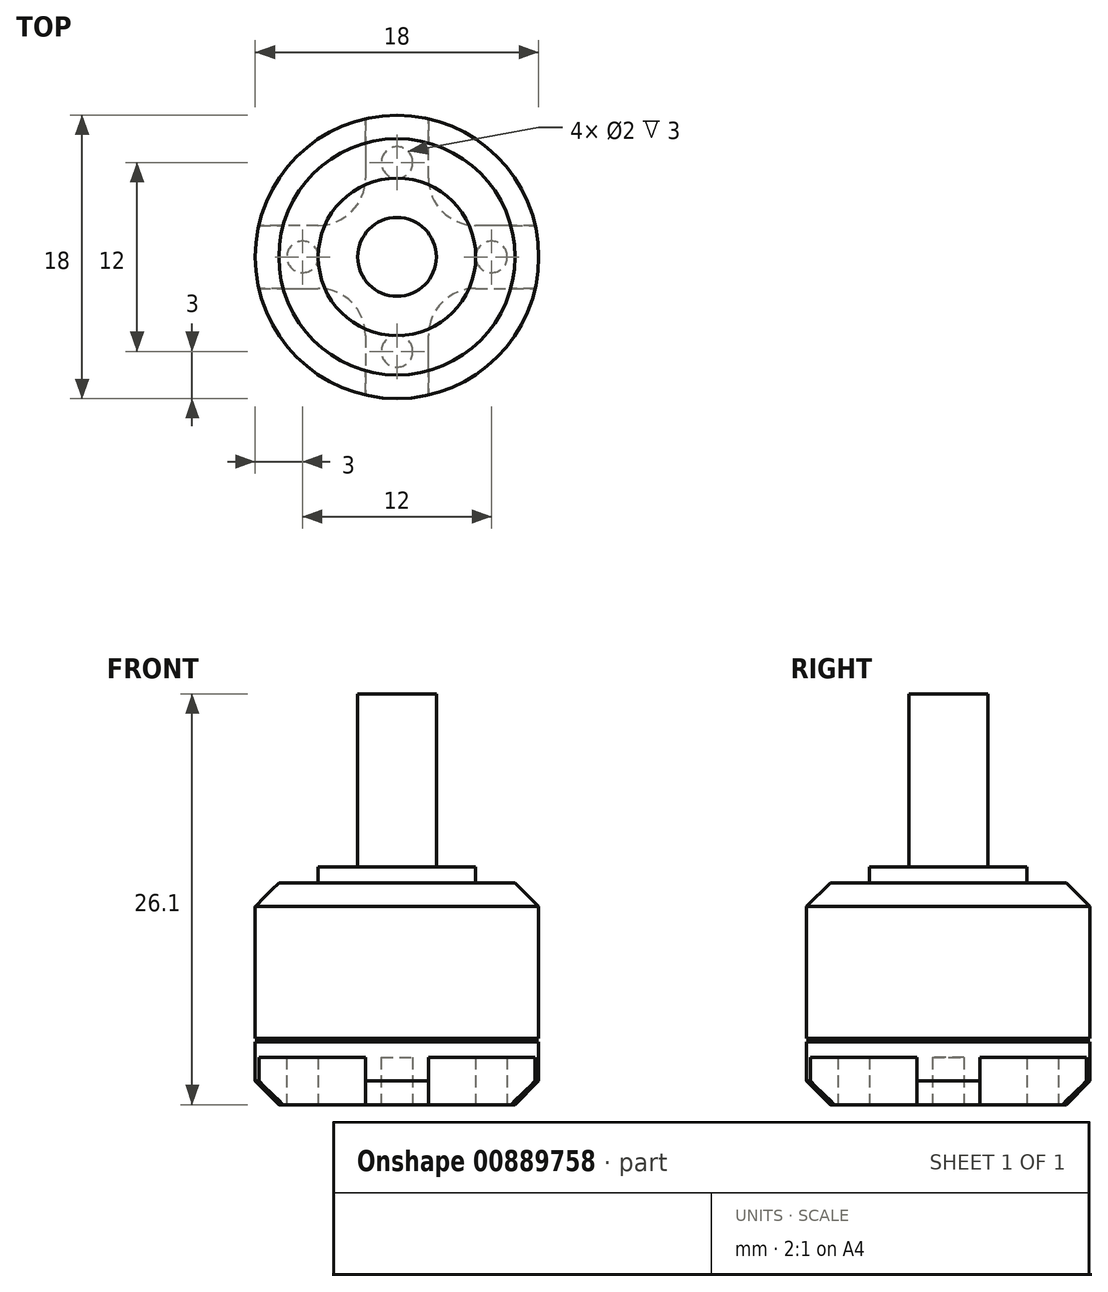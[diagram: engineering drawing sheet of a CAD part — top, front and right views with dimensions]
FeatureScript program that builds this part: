
annotation { "Feature Type Name" : "Feature", "Feature Type Description" : "" }
export const myFeature = defineFeature(function(context is Context, id is Id, definition is map)
    precondition{}
    {
        {
            var Q0;
            Q0=qCreatedBy(makeId("Front.planeOp"),FACE);
            var sketch = newSketch(context, id + "F0", { "sketchPlane" : qUnion([Q0])});
            skLineSegment(sketch, "E0", {"start": v(0, 19.43) * mm, "end": v(-2.5, 19.43) * mm});
            skLineSegment(sketch, "E1", {"start": v(-2.5, 19.43) * mm, "end": v(-2.5, 8.43) * mm});
            skLineSegment(sketch, "E2", {"start": v(-2.5, 8.43) * mm, "end": v(-5, 8.43) * mm});
            skLineSegment(sketch, "E3", {"start": v(-5, 8.43) * mm, "end": v(-5, 7.43) * mm});
            skLineSegment(sketch, "E4", {"start": v(-5, 7.43) * mm, "end": v(-7.5, 7.43) * mm});
            skLineSegment(sketch, "E5", {"start": v(-7.5, 7.43) * mm, "end": v(-9, 5.93) * mm});
            skLineSegment(sketch, "E6", {"start": v(-9, 5.93) * mm, "end": v(-9, -2.47) * mm});
            skLineSegment(sketch, "E7", {"start": v(-9, -2.47) * mm, "end": v(-2.5, -2.47) * mm});
            skLineSegment(sketch, "E8", {"start": v(-2.5, -2.47) * mm, "end": v(-2.5, -2.67) * mm});
            skLineSegment(sketch, "E9", {"start": v(-2.5, -2.67) * mm, "end": v(-9, -2.67) * mm});
            skLineSegment(sketch, "E10", {"start": v(-9, -2.67) * mm, "end": v(-9, -5.17) * mm});
            skLineSegment(sketch, "E11", {"start": v(-9, -5.17) * mm, "end": v(-7.5, -6.67) * mm});
            skLineSegment(sketch, "E12", {"start": v(-7.5, -6.67) * mm, "end": v(0, -6.67) * mm});
            skLineSegment(sketch, "E13", {"start": v(0, -6.67) * mm, "end": v(0, 19.43) * mm});
            skSolve(sketch);
        }
        {
            var Q0;
            Q0=qSketchRegion(id+"F0",true);
            var Q1;
            Q1=sQuery(id+"F0.wireOp",EDGE,"E13");
            revolve(context, id + "F1", {"entities" : qUnion([Q0]), "axis" : qUnion([Q1]), "revolveType" : RevolveType.FULL});
        }
        {
            var Q0;
            Q0=makeQuery(id+"F1.opRevolve","SWEPT_FACE",FACE,{"disambiguationData":[OSD([sQuery(id+"F0.wireOp",EDGE,"E12")])]});
            var sketch = newSketch(context, id + "F2", { "sketchPlane" : qUnion([Q0])});
            skCircle(sketch, "E14", {"center": v(0, 6) * mm, "radius": 1 * mm});
            skCircle(sketch, "E15.1.0", {"center": v(-6, 0) * mm, "radius": 1 * mm});
            skCircle(sketch, "E15.2.0", {"center": v(0, -6) * mm, "radius": 1 * mm});
            skPoint(sketch, "E15.center", {"position": v(0, 0) * mm});
            skCircle(sketch, "E16.1.3.0", {"center": v(6, 0) * mm, "radius": 1 * mm});
            skLineSegment(sketch, "E17", {"start": v(2, 16.04) * mm, "end": v(2, 5) * mm});
            skLineSegment(sketch, "E18", {"start": v(5, 2) * mm, "end": v(16.04, 2) * mm});
            skArc(sketch, "E19", {"start": v(16.04, 2) * mm, "mid": v(11.43, 11.43) * mm, "end": v(2, 16.04) * mm});
            skArc(sketch, "E20.filletArc", {"start": v(2, 5) * mm, "mid": v(2.88, 2.88) * mm, "end": v(5, 2) * mm});
            skLineSegment(sketch, "E21.1.0", {"start": v(-16.04, 2) * mm, "end": v(-5, 2) * mm});
            skArc(sketch, "E21.1.1", {"start": v(-5, 2) * mm, "mid": v(-2.88, 2.88) * mm, "end": v(-2, 5) * mm});
            skLineSegment(sketch, "E21.1.2", {"start": v(-2, 5) * mm, "end": v(-2, 16.04) * mm});
            skArc(sketch, "E21.1.3", {"start": v(-2, 16.04) * mm, "mid": v(-11.43, 11.43) * mm, "end": v(-16.04, 2) * mm});
            skLineSegment(sketch, "E21.2.0", {"start": v(-2, -16.04) * mm, "end": v(-2, -5) * mm});
            skArc(sketch, "E21.2.1", {"start": v(-2, -5) * mm, "mid": v(-2.88, -2.88) * mm, "end": v(-5, -2) * mm});
            skLineSegment(sketch, "E21.2.2", {"start": v(-5, -2) * mm, "end": v(-16.04, -2) * mm});
            skArc(sketch, "E21.2.3", {"start": v(-16.04, -2) * mm, "mid": v(-11.43, -11.43) * mm, "end": v(-2, -16.04) * mm});
            skArc(sketch, "E22.3.3.0", {"start": v(5, -2) * mm, "mid": v(2.88, -2.88) * mm, "end": v(2, -5) * mm});
            skLineSegment(sketch, "E22.6.3.0", {"start": v(16.04, -2) * mm, "end": v(5, -2) * mm});
            skLineSegment(sketch, "E22.7.3.0", {"start": v(2, -5) * mm, "end": v(2, -16.04) * mm});
            skArc(sketch, "E22.10.3.0", {"start": v(2, -16.04) * mm, "mid": v(11.43, -11.43) * mm, "end": v(16.04, -2) * mm});
            skSolve(sketch);
        }
        {
            var Q0;
            Q0=qSketchRegion(id+"F2",true);
            extrude(context, id + "F3", {"entities" : qUnion([Q0]), "operationType" : NewBodyOperationType.REMOVE, "oppositeDirection" : true, "depth" : 3 * mm});
        }
    });
